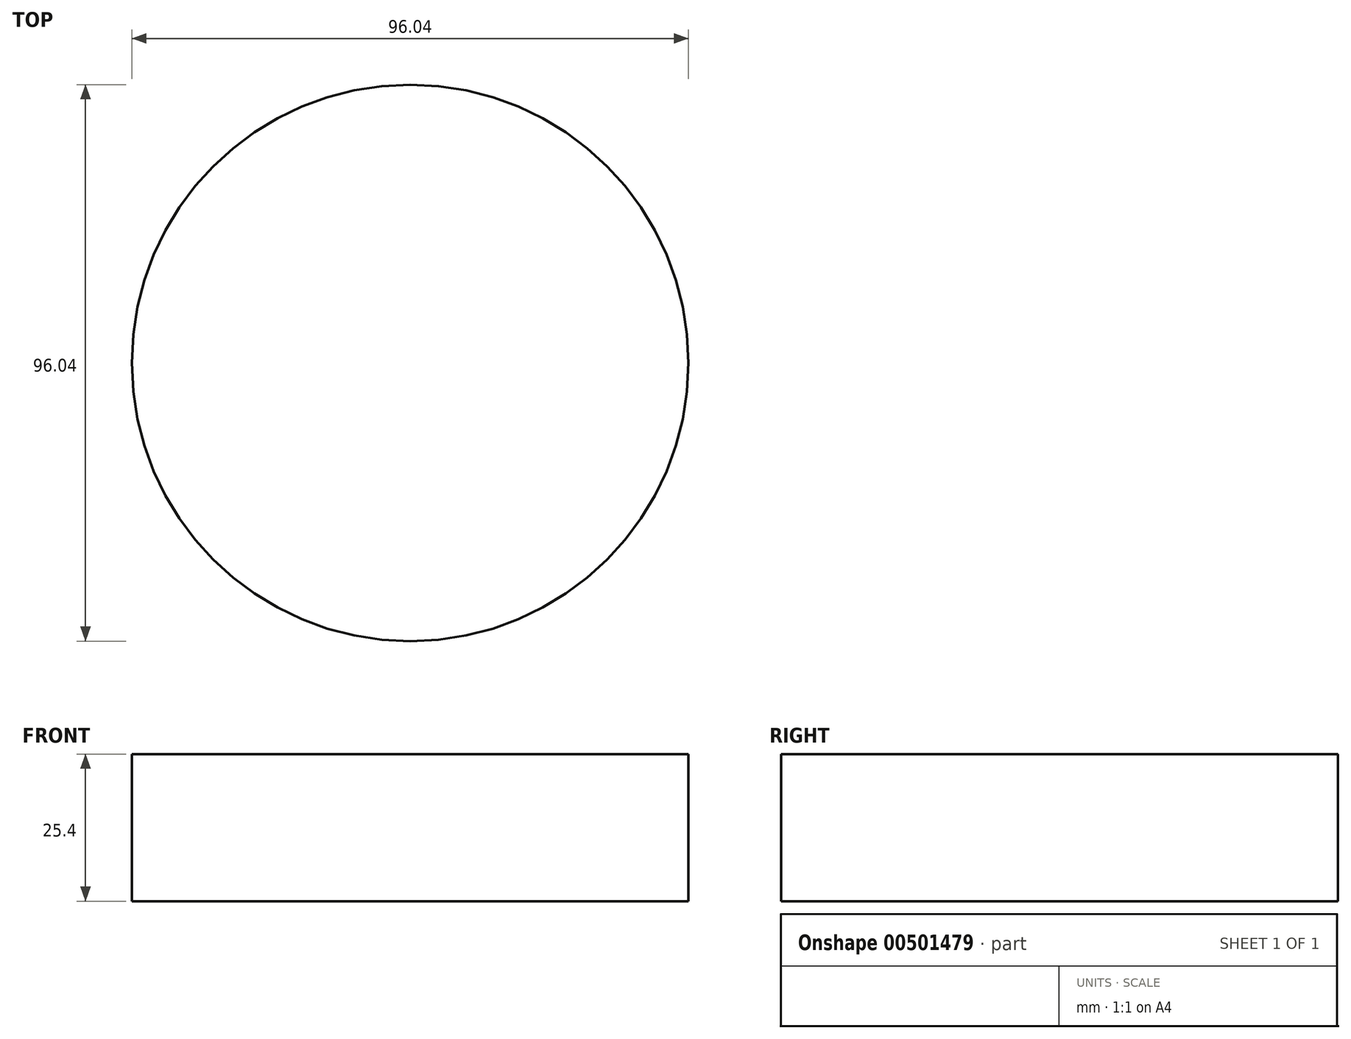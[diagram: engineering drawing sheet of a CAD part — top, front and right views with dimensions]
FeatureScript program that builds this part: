
annotation { "Feature Type Name" : "Feature", "Feature Type Description" : "" }
export const myFeature = defineFeature(function(context is Context, id is Id, definition is map)
    precondition{}
    {
        {
            var Q0;
            Q0=qCreatedBy(makeId("Top.planeOp"),FACE);
            var sketch = newSketch(context, id + "F0", { "sketchPlane" : qUnion([Q0])});
            skCircle(sketch, "E0", {"center": v(0, 0) * mm, "radius": 48.02 * mm});
            skSolve(sketch);
        }
        {
            var Q0;
            Q0 = qSketchRegion(id + "F0", true);
            extrude(context, id + "F1", {"entities" : qUnion([Q0]), "depth" : 25.4 * mm});
        }
    });
